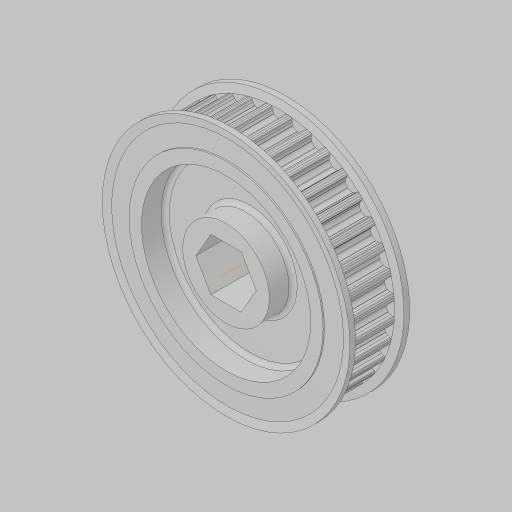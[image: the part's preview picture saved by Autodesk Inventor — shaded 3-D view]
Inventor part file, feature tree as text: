
AUTODESK INVENTOR PART (.ipt)
format: ipt  version: 2023.5 (Build 275446000, 446)  size: 818,176 bytes
history: native  units: in
note: dims shown in document units (in); Inventor stores cm internally (conversion verified against a paired STEP export)
features: mirror x1
ambient origin geometry x8: Origin, YZ Plane, XZ Plane, XY Plane, X Axis, Y Axis, Z Axis, Center Point
bodies: Solid1 (feature_tree)
feature tree (1):
  mirror  "Mirror1"
